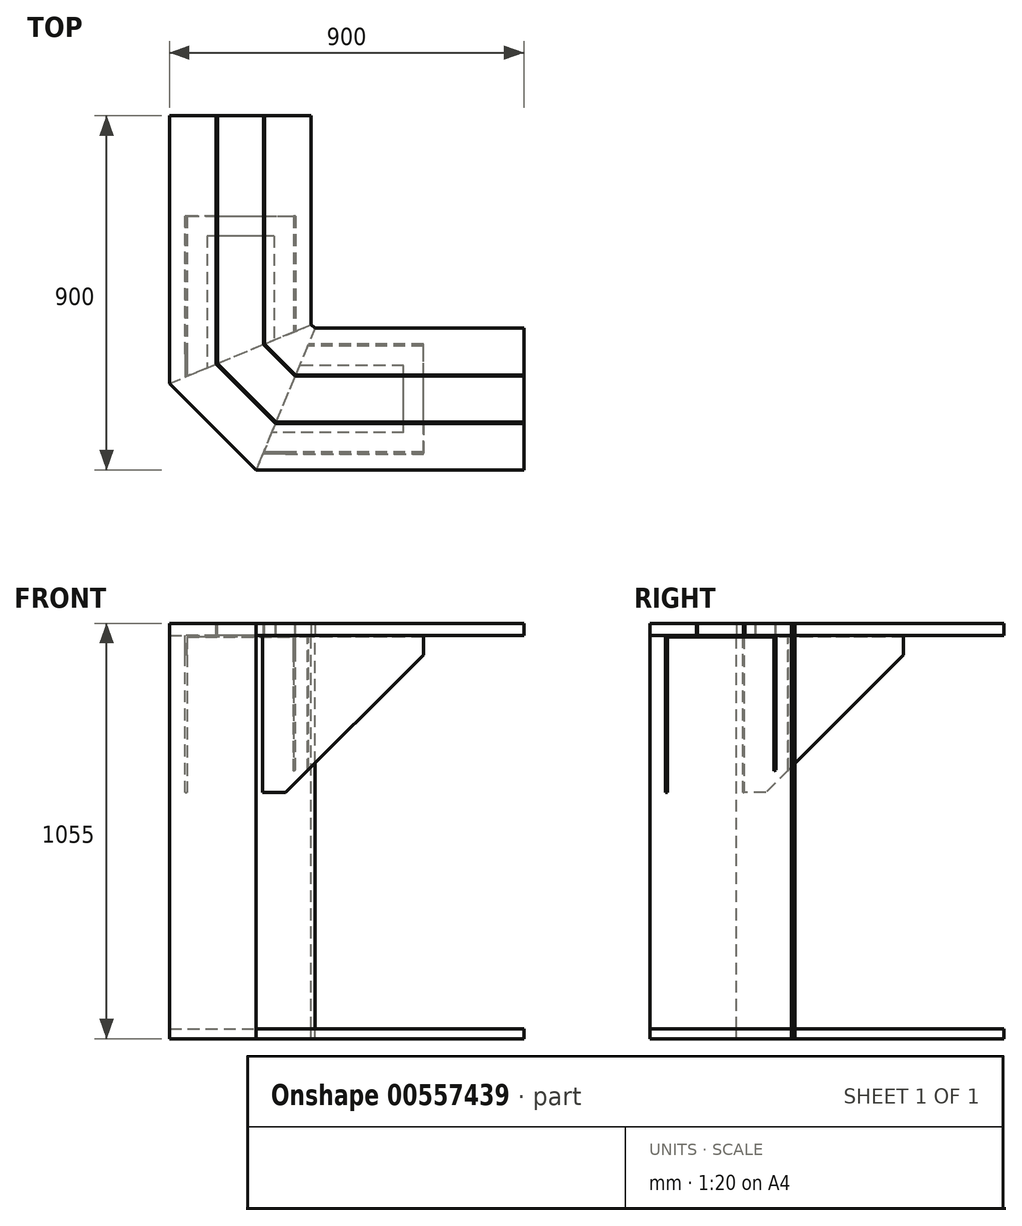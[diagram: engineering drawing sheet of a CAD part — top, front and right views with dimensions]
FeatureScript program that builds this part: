
annotation { "Feature Type Name" : "Feature", "Feature Type Description" : "" }
export const myFeature = defineFeature(function(context is Context, id is Id, definition is map)
    precondition{}
    {
        {
            var Q0;
            Q0=qCreatedBy(makeId("Top.planeOp"),FACE);
            var sketch = newSketch(context, id + "F0", { "sketchPlane" : qUnion([Q0])});
            skLineSegment(sketch, "E0", {"start": v(0, 65.76) * mm, "end": v(0, -55.36) * mm, "construction": true});
            skLineSegment(sketch, "E1.bottom", {"start": v(-550, 550) * mm, "end": v(350, 550) * mm, "construction": true});
            skLineSegment(sketch, "E1.top", {"start": v(-550, -350) * mm, "end": v(350, -350) * mm, "construction": true});
            skLineSegment(sketch, "E1.left", {"start": v(-550, 550) * mm, "end": v(-550, -350) * mm, "construction": true});
            skLineSegment(sketch, "E1.right", {"start": v(350, 550) * mm, "end": v(350, -350) * mm, "construction": true});
            skLineSegment(sketch, "E2", {"start": v(-550, 550) * mm, "end": v(-550, -130) * mm});
            skLineSegment(sketch, "E3", {"start": v(-550, -130) * mm, "end": v(-330, -350) * mm});
            skLineSegment(sketch, "E4", {"start": v(-330, -350) * mm, "end": v(350, -350) * mm});
            skLineSegment(sketch, "E5", {"start": v(-550, 550) * mm, "end": v(-190, 550) * mm});
            skLineSegment(sketch, "E6", {"start": v(350, -350) * mm, "end": v(350, 10) * mm});
            skLineSegment(sketch, "E7.0", {"start": v(-190, 19.12) * mm, "end": v(-180.88, 10) * mm});
            skLineSegment(sketch, "E8", {"start": v(-190, 550) * mm, "end": v(-190, 19.12) * mm});
            skLineSegment(sketch, "E9", {"start": v(350, 10) * mm, "end": v(-180.88, 10) * mm});
            skSolve(sketch);
        }
        {
            var Q0;
            Q0 = qSketchRegion(id + "F0", true);
            extrude(context, id + "F1", {"entities" : qUnion([Q0]), "depth" : 30 * mm, "offsetDistance" : 25 * mm});
        }
        {
            var Q0;
            Q0=makeQuery(id+"F1.opExtrude","CAP_FACE",FACE,{"disambiguationData":[OSD([sQuery(id+"F0.wireOp",EDGE,"E2"),sQuery(id+"F0.wireOp",EDGE,"E3"),sQuery(id+"F0.wireOp",EDGE,"E4"),sQuery(id+"F0.wireOp",EDGE,"E5"),sQuery(id+"F0.wireOp",EDGE,"E6"),sQuery(id+"F0.wireOp",EDGE,"E7.0"),sQuery(id+"F0.wireOp",EDGE,"E8"),sQuery(id+"F0.wireOp",EDGE,"E9")])],"isStart":true});
            var sketch = newSketch(context, id + "F2", { "sketchPlane" : qUnion([Q0])});
            skLineSegment(sketch, "E10.0", {"start": v(-550, 130) * mm, "end": v(-330, 350) * mm});
            skLineSegment(sketch, "E10.1", {"start": v(-190, -19.12) * mm, "end": v(-180.88, -10) * mm});
            skLineSegment(sketch, "E11", {"start": v(-550, 130) * mm, "end": v(-190, -19.12) * mm});
            skLineSegment(sketch, "E12", {"start": v(-180.88, -10) * mm, "end": v(-330, 350) * mm});
            skSolve(sketch);
        }
        {
            var Q0;
            Q0 = qSketchRegion(id + "F2", true);
            extrude(context, id + "F3", {"entities" : qUnion([Q0]), "operationType" : NewBodyOperationType.ADD, "depth" : 1000 * mm, "offsetDistance" : 25 * mm});
        }
        {
            var Q0;
            Q0=makeQuery(id+"F3.opExtrude","CAP_FACE",FACE,{"disambiguationData":[OSD([sQuery(id+"F2.wireOp",EDGE,"E10.0"),sQuery(id+"F2.wireOp",EDGE,"E10.1"),sQuery(id+"F2.wireOp",EDGE,"E11"),sQuery(id+"F2.wireOp",EDGE,"E12")])],"isStart":false});
            var sketch = newSketch(context, id + "F4", { "sketchPlane" : qUnion([Q0])});
            skLineSegment(sketch, "E13.0", {"start": v(-330, 350) * mm, "end": v(350, 350) * mm});
            skLineSegment(sketch, "E13.1", {"start": v(-550, 130) * mm, "end": v(-330, 350) * mm});
            skLineSegment(sketch, "E13.2", {"start": v(-550, -550) * mm, "end": v(-550, 130) * mm});
            skLineSegment(sketch, "E13.3", {"start": v(-550, -550) * mm, "end": v(-190, -550) * mm});
            skLineSegment(sketch, "E13.4", {"start": v(350, 350) * mm, "end": v(350, -10) * mm});
            skLineSegment(sketch, "E14.0", {"start": v(350, -10) * mm, "end": v(-180.88, -10) * mm});
            skLineSegment(sketch, "E14.1", {"start": v(-190, -19.12) * mm, "end": v(-180.88, -10) * mm});
            skLineSegment(sketch, "E14.2", {"start": v(-190, -550) * mm, "end": v(-190, -19.12) * mm});
            skSolve(sketch);
        }
        {
            var Q0;
            Q0 = qSketchRegion(id + "F4", true);
            extrude(context, id + "F5", {"entities" : qUnion([Q0]), "operationType" : NewBodyOperationType.ADD, "depth" : 25 * mm, "offsetDistance" : 25 * mm});
        }
        {
            var Q0;
            {var subQ0=sQuery(id+"F0.wireOp",EDGE,"E7.0");var subQ1=sQuery(id+"F0.wireOp",EDGE,"E6");var subQ2=sQuery(id+"F0.wireOp",EDGE,"E4");var subQ3=sQuery(id+"F0.wireOp",EDGE,"E3");var subQ4=sQuery(id+"F0.wireOp",EDGE,"E9");Q0=makeQuery(id+"F3.boolean.opBoolean","SPLIT",FACE,{"disambiguationData":[TD([makeQuery(id+"F1.opExtrude","SWEPT_FACE",FACE,{"disambiguationData":[OSD([subQ2])]})])],"derivedFrom":makeQuery(id+"F1.opExtrude","CAP_FACE",FACE,{"disambiguationData":[OSD([sQuery(id+"F0.wireOp",EDGE,"E2"),subQ3,subQ2,sQuery(id+"F0.wireOp",EDGE,"E5"),subQ1,subQ0,sQuery(id+"F0.wireOp",EDGE,"E8"),subQ4])],"isStart":true})});}
            var sketch = newSketch(context, id + "F6", { "sketchPlane" : qUnion([Q0])});
            skLineSegment(sketch, "E15", {"start": v(-255.44, 170) * mm, "end": v(350, 170) * mm, "construction": true});
            skLineSegment(sketch, "E16.bottom", {"start": v(94.65, 305) * mm, "end": v(-311.36, 305) * mm});
            skLineSegment(sketch, "E16.top", {"start": v(94.65, 310) * mm, "end": v(-313.43, 310) * mm});
            skLineSegment(sketch, "E16.left", {"start": v(94.65, 305) * mm, "end": v(94.65, 310) * mm});
            skPoint(sketch, "E17.0", {"position": v(-440, 240) * mm});
            skPoint(sketch, "E17.1", {"position": v(-185.44, -14.56) * mm});
            skLineSegment(sketch, "E18", {"start": v(-185.44, -14.56) * mm, "end": v(-440, 240) * mm, "construction": true});
            skLineSegment(sketch, "E19.MirrorCS", {"start": v(-505, 113.43) * mm, "end": v(-510, 113.43) * mm});
            skLineSegment(sketch, "E20.MirrorCS", {"start": v(-505, -294.65) * mm, "end": v(-510, -294.65) * mm});
            skLineSegment(sketch, "E21.MirrorCS", {"start": v(-510, -294.65) * mm, "end": v(-510, 113.43) * mm});
            skLineSegment(sketch, "E22.MirrorCS", {"start": v(-505, -294.65) * mm, "end": v(-505, 113.43) * mm});
            skLineSegment(sketch, "E23.MirrorCS", {"start": v(94.65, 35) * mm, "end": v(94.65, 30) * mm});
            skLineSegment(sketch, "E24.MirrorCS", {"start": v(94.65, 35) * mm, "end": v(-199.52, 35) * mm});
            skLineSegment(sketch, "E25.MirrorCS", {"start": v(94.65, 30) * mm, "end": v(-197.45, 30) * mm});
            skLineSegment(sketch, "E26.0", {"start": v(-197.45, 30) * mm, "end": v(-199.52, 35) * mm});
            skPoint(sketch, "E27.MirrorCS.end.orphan", {"position": v(-313.43, 30) * mm});
            skPoint(sketch, "E27.MirrorCS.start.orphan", {"position": v(-313.43, 35) * mm});
            skPoint(sketch, "E28.orphan", {"position": v(-313.43, 305) * mm});
            skPoint(sketch, "E29.orphan", {"position": v(-330, 350) * mm});
            skLineSegment(sketch, "E30.trimOffspring", {"start": v(-311.36, 305) * mm, "end": v(-313.43, 310) * mm});
            skPoint(sketch, "E31.orphan", {"position": v(-180.88, -10) * mm});
            skLineSegment(sketch, "E32.MirrorCS", {"start": v(-235, -294.65) * mm, "end": v(-230, -294.65) * mm});
            skLineSegment(sketch, "E33.MirrorCS", {"start": v(-230, -2.55) * mm, "end": v(-235, -0.48) * mm});
            skLineSegment(sketch, "E34.MirrorCS", {"start": v(-235, -294.65) * mm, "end": v(-235, -0.48) * mm});
            skLineSegment(sketch, "E35.MirrorCS", {"start": v(-230, -294.65) * mm, "end": v(-230, -2.55) * mm});
            skPoint(sketch, "E36.MirrorP", {"position": v(-190, -19.12) * mm});
            skSolve(sketch);
        }
        {
            var Q0;
            Q0 = qSketchRegion(id + "F6", true);
            extrude(context, id + "F7", {"entities" : qUnion([Q0]), "operationType" : NewBodyOperationType.ADD, "depth" : 400 * mm, "offsetDistance" : 25 * mm});
        }
        {
            var Q0;
            Q0=makeQuery(id+"F7.opExtrude","CAP_EDGE",EDGE,{"disambiguationData":[OSD([sQuery(id+"F6.wireOp",EDGE,"E20.MirrorCS")])],"isStart":false});
            var Q1;
            Q1=makeQuery(id+"F7.opExtrude","CAP_EDGE",EDGE,{"disambiguationData":[OSD([sQuery(id+"F6.wireOp",EDGE,"E16.left")])],"isStart":false});
            var Q2;
            Q2=makeQuery(id+"F7.opExtrude","CAP_EDGE",EDGE,{"disambiguationData":[OSD([sQuery(id+"F6.wireOp",EDGE,"E32.MirrorCS")])],"isStart":false});
            var Q3;
            Q3=makeQuery(id+"F7.opExtrude","CAP_EDGE",EDGE,{"disambiguationData":[OSD([sQuery(id+"F6.wireOp",EDGE,"E23.MirrorCS")])],"isStart":false});
            chamfer(context, id + "F8", {"entities" : qUnion([Q0, Q1, Q2, Q3]), "width" : 350 * mm, "tangentPropagation" : true});
        }
        {
            var Q0;
            {var subQ0=sQuery(id+"F0.wireOp",EDGE,"E7.0");var subQ1=sQuery(id+"F0.wireOp",EDGE,"E6");var subQ2=sQuery(id+"F0.wireOp",EDGE,"E4");var subQ3=sQuery(id+"F0.wireOp",EDGE,"E3");var subQ4=sQuery(id+"F0.wireOp",EDGE,"E9");Q0=makeQuery(id+"F3.boolean.opBoolean","SPLIT",FACE,{"disambiguationData":[TD([makeQuery(id+"F1.opExtrude","SWEPT_FACE",FACE,{"disambiguationData":[OSD([subQ2])]})])],"derivedFrom":makeQuery(id+"F1.opExtrude","CAP_FACE",FACE,{"disambiguationData":[OSD([sQuery(id+"F0.wireOp",EDGE,"E2"),subQ3,subQ2,sQuery(id+"F0.wireOp",EDGE,"E5"),subQ1,subQ0,sQuery(id+"F0.wireOp",EDGE,"E8"),subQ4])],"isStart":true})});}
            var sketch = newSketch(context, id + "F9", { "sketchPlane" : qUnion([Q0])});
            skLineSegment(sketch, "E37.0", {"start": v(94.65, 305) * mm, "end": v(-311.36, 305) * mm});
            skLineSegment(sketch, "E38", {"start": v(94.65, 305) * mm, "end": v(94.65, 255) * mm});
            skLineSegment(sketch, "E39", {"start": v(44.65, 255) * mm, "end": v(-290.65, 255) * mm});
            skPoint(sketch, "E40.orphan", {"position": v(-180.88, -10) * mm});
            skPoint(sketch, "E37.2.end.orphan", {"position": v(94.65, 310) * mm});
            skPoint(sketch, "E41.0", {"position": v(-185.44, -14.56) * mm});
            skPoint(sketch, "E41.1", {"position": v(-440, 240) * mm});
            skLineSegment(sketch, "E42", {"start": v(-440, 240) * mm, "end": v(-185.44, -14.56) * mm, "construction": true});
            skLineSegment(sketch, "E43.0", {"start": v(-199.52, 35) * mm, "end": v(-220.23, 85) * mm});
            skLineSegment(sketch, "E44.0", {"start": v(94.65, 35) * mm, "end": v(-199.52, 35) * mm});
            skLineSegment(sketch, "E45", {"start": v(94.65, 35) * mm, "end": v(94.65, 85) * mm});
            skLineSegment(sketch, "E46", {"start": v(44.65, 85) * mm, "end": v(-220.23, 85) * mm});
            skLineSegment(sketch, "E47.trimOffspring", {"start": v(-290.65, 255) * mm, "end": v(-311.36, 305) * mm});
            skLineSegment(sketch, "E48.MirrorCS", {"start": v(-235, -294.65) * mm, "end": v(-285, -294.65) * mm});
            skLineSegment(sketch, "E49.MirrorCS", {"start": v(-235, -294.65) * mm, "end": v(-235, -0.48) * mm});
            skLineSegment(sketch, "E50.MirrorCS", {"start": v(-455, 90.65) * mm, "end": v(-505, 111.36) * mm});
            skLineSegment(sketch, "E51.MirrorCS", {"start": v(-505, -294.65) * mm, "end": v(-505, 111.36) * mm});
            skPoint(sketch, "E52.MirrorP", {"position": v(-510, -294.65) * mm});
            skLineSegment(sketch, "E53.MirrorCS", {"start": v(-285, -244.65) * mm, "end": v(-285, 20.23) * mm});
            skLineSegment(sketch, "E54.MirrorCS", {"start": v(-455, -244.65) * mm, "end": v(-455, 90.65) * mm});
            skLineSegment(sketch, "E55.MirrorCS", {"start": v(-505, -294.65) * mm, "end": v(-455, -294.65) * mm});
            skLineSegment(sketch, "E56.MirrorCS", {"start": v(-235, -0.48) * mm, "end": v(-285, 20.23) * mm});
            skLineSegment(sketch, "E57", {"start": v(-285, -294.65) * mm, "end": v(-455, -294.65) * mm});
            skLineSegment(sketch, "E58", {"start": v(-285, -244.65) * mm, "end": v(-455, -244.65) * mm});
            skLineSegment(sketch, "E59", {"start": v(94.65, 85) * mm, "end": v(94.65, 255) * mm});
            skLineSegment(sketch, "E60", {"start": v(44.65, 255) * mm, "end": v(44.65, 85) * mm});
            skSolve(sketch);
        }
        {
            var Q0;
            Q0=makeQuery(id+"F1.opExtrude","CAP_FACE",FACE,{"disambiguationData":[OSD([sQuery(id+"F0.wireOp",EDGE,"E2"),sQuery(id+"F0.wireOp",EDGE,"E3"),sQuery(id+"F0.wireOp",EDGE,"E4"),sQuery(id+"F0.wireOp",EDGE,"E5"),sQuery(id+"F0.wireOp",EDGE,"E6"),sQuery(id+"F0.wireOp",EDGE,"E7.0"),sQuery(id+"F0.wireOp",EDGE,"E8"),sQuery(id+"F0.wireOp",EDGE,"E9")])],"isStart":false});
            var sketch = newSketch(context, id + "F10", { "sketchPlane" : qUnion([Q0])});
            skSolve(sketch);
        }
        {
            var Q0;
            Q0=makeQuery(id+"F10.imprint","IMPRINT",FACE,{"disambiguationData":[TD([[makeQuery(id+"F10.imprint","IMPRINT",EDGE,{"derivedFrom":makeQuery(id+"F1.opExtrude","CAP_EDGE",EDGE,{"disambiguationData":[OSD([sQuery(id+"F0.wireOp",EDGE,"E2")])],"isStart":false})}),1.0]])]});
            var sketch = newSketch(context, id + "F11", { "sketchPlane" : qUnion([Q0])});
            skLineSegment(sketch, "E61.0", {"start": v(-280.3, -230) * mm, "end": v(350, -230) * mm, "construction": true});
            skLineSegment(sketch, "E61.1", {"start": v(-430, -80.3) * mm, "end": v(-280.3, -230) * mm, "construction": true});
            skLineSegment(sketch, "E61.2", {"start": v(-430, 550) * mm, "end": v(-430, -80.3) * mm, "construction": true});
            skLineSegment(sketch, "E62.0", {"start": v(-230.59, -110) * mm, "end": v(350, -110) * mm, "construction": true});
            skLineSegment(sketch, "E62.1", {"start": v(-310, -30.59) * mm, "end": v(-230.59, -110) * mm, "construction": true});
            skLineSegment(sketch, "E62.2", {"start": v(-310, 550) * mm, "end": v(-310, -30.59) * mm, "construction": true});
            skLineSegment(sketch, "E63.0", {"start": v(-280.92, -231.5) * mm, "end": v(350, -231.5) * mm});
            skLineSegment(sketch, "E63.1", {"start": v(-431.5, -80.92) * mm, "end": v(-280.92, -231.5) * mm});
            skLineSegment(sketch, "E63.2", {"start": v(-431.5, 550) * mm, "end": v(-431.5, -80.92) * mm});
            skLineSegment(sketch, "E64.0", {"start": v(-279.67, -228.5) * mm, "end": v(350, -228.5) * mm});
            skLineSegment(sketch, "E64.1", {"start": v(-428.5, -79.67) * mm, "end": v(-279.67, -228.5) * mm});
            skLineSegment(sketch, "E64.2", {"start": v(-428.5, 550) * mm, "end": v(-428.5, -79.67) * mm});
            skLineSegment(sketch, "E65.0", {"start": v(-231.21, -111.5) * mm, "end": v(350, -111.5) * mm});
            skLineSegment(sketch, "E65.1", {"start": v(-311.5, -31.21) * mm, "end": v(-231.21, -111.5) * mm});
            skLineSegment(sketch, "E65.2", {"start": v(-311.5, 550) * mm, "end": v(-311.5, -31.21) * mm});
            skLineSegment(sketch, "E66.0", {"start": v(-229.97, -108.5) * mm, "end": v(350, -108.5) * mm});
            skLineSegment(sketch, "E66.1", {"start": v(-308.5, -29.97) * mm, "end": v(-229.97, -108.5) * mm});
            skLineSegment(sketch, "E66.2", {"start": v(-308.5, 550) * mm, "end": v(-308.5, -29.97) * mm});
            skLineSegment(sketch, "E67", {"start": v(350, -228.5) * mm, "end": v(350, -231.5) * mm});
            skLineSegment(sketch, "E68", {"start": v(350, -108.5) * mm, "end": v(350, -111.5) * mm});
            skLineSegment(sketch, "E69", {"start": v(-308.5, 550) * mm, "end": v(-311.5, 550) * mm});
            skLineSegment(sketch, "E70", {"start": v(-428.5, 550) * mm, "end": v(-431.5, 550) * mm});
            skSolve(sketch);
        }
        {
            var Q0;
            Q0 = qSketchRegion(id + "F11", true);
            var Q1;
            {var subQ0=sQuery(id+"F0.wireOp",EDGE,"E7.0");var subQ1=sQuery(id+"F0.wireOp",EDGE,"E3");var subQ2=sQuery(id+"F0.wireOp",EDGE,"E5");var subQ3=sQuery(id+"F0.wireOp",EDGE,"E2");var subQ4=sQuery(id+"F0.wireOp",EDGE,"E8");Q1=makeQuery(id+"F3.boolean.opBoolean","SPLIT",FACE,{"disambiguationData":[TD([makeQuery(id+"F1.opExtrude","SWEPT_FACE",FACE,{"disambiguationData":[OSD([subQ3])]})])],"derivedFrom":makeQuery(id+"F1.opExtrude","CAP_FACE",FACE,{"disambiguationData":[OSD([subQ3,subQ1,sQuery(id+"F0.wireOp",EDGE,"E4"),subQ2,sQuery(id+"F0.wireOp",EDGE,"E6"),subQ0,subQ4,sQuery(id+"F0.wireOp",EDGE,"E9")])],"isStart":true})});}
            extrude(context, id + "F12", {"entities" : qUnion([Q0]), "operationType" : NewBodyOperationType.REMOVE, "endBound" : BoundingType.UP_TO_SURFACE, "oppositeDirection" : true, "depth" : 25 * mm, "endBoundEntityFace" : qUnion([Q1]), "offsetDistance" : 25 * mm});
        }
        {
            var Q0;
            Q0 = qSketchRegion(id + "F9", true);
            extrude(context, id + "F13", {"entities" : qUnion([Q0]), "operationType" : NewBodyOperationType.ADD, "depth" : 5 * mm, "offsetDistance" : 25 * mm});
        }
    });
